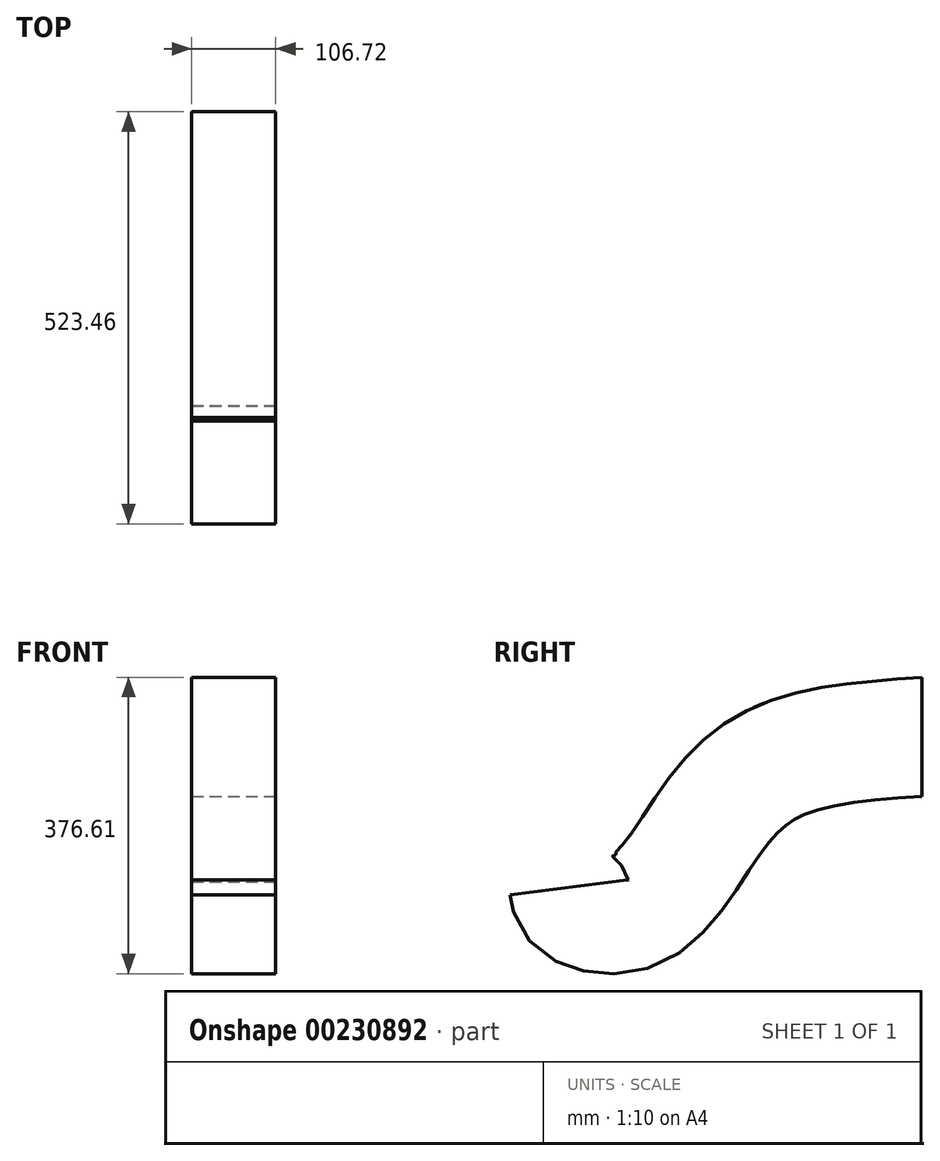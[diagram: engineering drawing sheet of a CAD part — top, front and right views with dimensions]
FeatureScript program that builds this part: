
annotation { "Feature Type Name" : "Feature", "Feature Type Description" : "" }
export const myFeature = defineFeature(function(context is Context, id is Id, definition is map)
    precondition{}
    {
        {
            var Q0;
            Q0=qCreatedBy(makeId("Front.planeOp"),FACE);
            var sketch = newSketch(context, id + "F0", { "sketchPlane" : qUnion([Q0])});
            skLineSegment(sketch, "E0.bottom", {"start": v(-53.3, 76.06) * mm, "end": v(53.41, 76.06) * mm});
            skLineSegment(sketch, "E0.top", {"start": v(-53.3, -74.94) * mm, "end": v(53.41, -74.94) * mm});
            skLineSegment(sketch, "E0.left", {"start": v(-53.3, 76.06) * mm, "end": v(-53.3, -74.94) * mm});
            skLineSegment(sketch, "E0.right", {"start": v(53.41, 76.06) * mm, "end": v(53.41, -74.94) * mm});
            skSolve(sketch);
        }
        {
            var Q0;
            Q0=qCreatedBy(makeId("Right.planeOp"),FACE);
            var sketch = newSketch(context, id + "F1", { "sketchPlane" : qUnion([Q0])});
            skFitSpline(sketch, "E1", {"points": [v(0, 0) * mm, v(-170.73, -26.47) * mm, v(-263.49, -101.27) * mm, v(-362.31, -218.77) * mm, v(-437.84, -213.51) * mm, v(-449.1, -191.02) * mm], "startDerivative": vector(-711.81, -50.76) * mm, "endDerivative": vector(-47.92, 239.93) * mm});
            skSolve(sketch);
        }
        {
            var Q0;
            Q0=makeQuery(id+"F0.imprint","IMPRINT",FACE,{"disambiguationData":[TD([[makeQuery(id+"F0.imprint","IMPRINT",EDGE,{"derivedFrom":sQuery(id+"F0.wireOp",EDGE,"E0.bottom")}),-1.0]])]});
            var Q1;
            Q1 = qConstructionFilter(qBodyType(qCreatedBy(id + "F1" ,EDGE), BodyType.WIRE), ConstructionObject.NO);
            sweep(context, id + "F2", {"profiles" : qUnion([Q0]), "path" : qUnion([Q1])});
        }
    });
